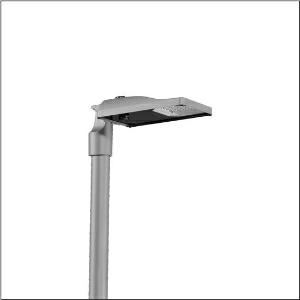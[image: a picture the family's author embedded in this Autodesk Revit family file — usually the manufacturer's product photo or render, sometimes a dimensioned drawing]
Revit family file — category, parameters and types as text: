
# Revit family: streetlight_sl_31_micro___pl52_5xh5h31t08ca_bf49
name_source: partatom
category: Lighting Fixtures
units: mm (PartAtom-declared; Revit-internal decimal feet)

## family parameters
Cut with Voids When Loaded = No
Host = Face
Light Source = No
Part Type = Normal
Room Calculation Point = No
Round Connector Dimension = Use Diameter
Shared = No

## types (1)
- --- (1 x LED, 1420 lm, 10.2 W, 3000K)
    Apparent Load = 10 VA
    CIE Flux Codes = 27 59 98 100 100
    Color Rendering = 70
    Color Temperature = 3000K
    Default Elevation = 1800 mm
    Description = Streetlight SL 31 micro, mast luminaire, primary light control with lens, of PMMA, primary optical cover: cover, of toughened safety glass, transparent, light distribution: PL52, light emission: direct distribution, primary light characteristic: asymmetric, installation type: post-top, side-entry, LED, High Power LED, rated luminous flux: 1.420lm, luminous efficacy: 139lm/W, light colour: 730, colour temperature: 3000K, control: presetting dimming logarithmic, flexible luminous flux parameterisation, time-dependent luminous flux control, constant luminous flux control, power reduction, intelligent temperature release in ECG and LED module, overheat protection, with cable H07RN-F 2x 1.5mm², mains connection: 220..240V, AC, 50/60Hz, connection cable pre-assembled, cable length: 5,5m, start of lifetime: 10W, end of service life: 11W, reduction: 5W, luminaire housing, of diecast aluminium, powder-coated, Siteco® metallic grey (DB 702S), corrosivity category C5 high according to DIN EN ISO 12944, sealing non-destructively replaceable, multi-level sealing system, mast flange (76/60mm) included as standard, inclination: -15°..+20° (post-top) | -20°..+20° (side-entry), adjustable in 5° steps, no sealing on luminaire upper side, Smart Interface below and above, protection rating (complete): IP66, insulation class (complete): insulation class II (safety insulation), certification: CE, ENEC, ENEC+, VDE, UKCA, ZD4i, impact resistance: IK09, permissible operating ambient temperature for outdoor applications: -40..+50°C, standard-compliant lighting for roads and squares, packaging unit: 1 piece

Light Distribution: PL52
    Height = 76 mm
    Lamp = 1 x LED
    Lamp Light Flux = 1420 lm
    Lamp Power = 10.2 W
    Lamp count = 1
    Length = 467 mm
    Luminous efficacy = 139 lm/W
    Manufacturer = Siteco
    ModVariant = No
    Model = 5XH5H31T08CA
    Number of Poles = 1
    OnlyDefault = Yes
    Power Factor = 1
    Product Name = Streetlight SL 31 micro | PL52
    Product group = mast luminaire | pylon top
    ProductGroupID = 6100
    Protection Class = Protection class II
    Protection Degree = IP 66
    RLX_Detail_Level = 1
    RLX_Emergency_Light_Flux = 0 lm
    RLX_Emergency_Type = 0
    RLX_Emergency_Type_DB = No
    RlxData = <blob elided: 54169 chars, md5=5205925f>
    Socket = socket
    Standby Power = 0 W
    System Light Flux = 1420 lm
    System Power = 10 W
    Type Comments = factory setting: luminous flux: 100 % | dim-lin: 254 | 386 mA
    Type Image = l_1300315.jpg
    URL = http://relux.com
    VarID = @adj_006173
    Voltage = 0 V
    Weight = 0.00 kg
    Width = 265 mm

## geometry (parser evidence)
native form markers: Blend x4, Sweep x13
no freeform markers — native parametric forms only
